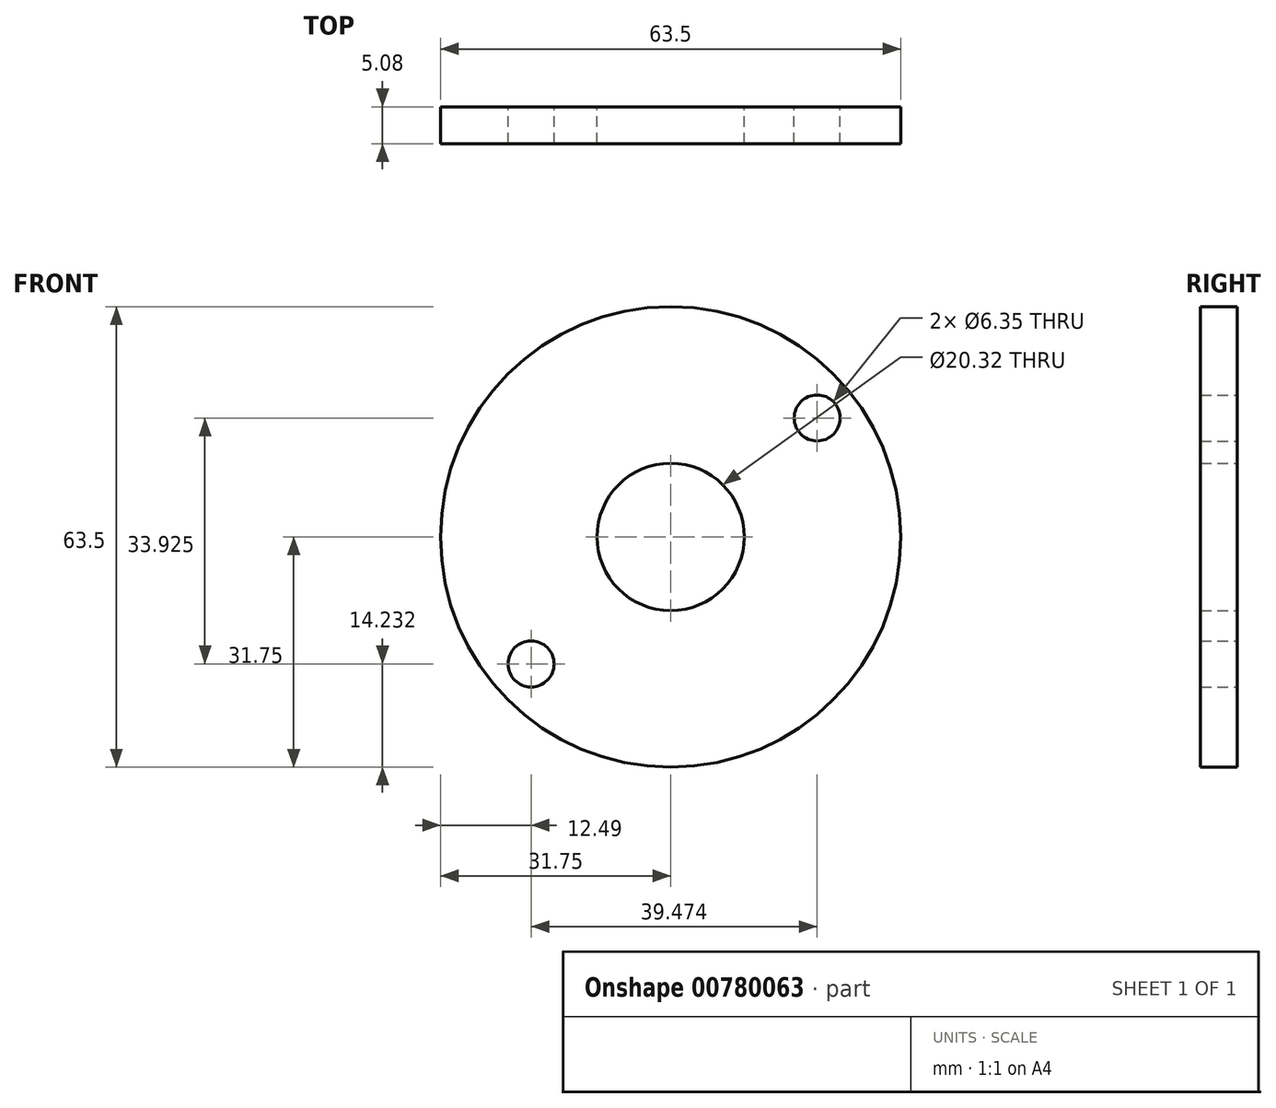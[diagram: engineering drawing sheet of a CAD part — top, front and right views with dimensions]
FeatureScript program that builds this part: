
annotation { "Feature Type Name" : "Feature", "Feature Type Description" : "" }
export const myFeature = defineFeature(function(context is Context, id is Id, definition is map)
    precondition{}
    {
        {
            var Q0;
            Q0=qCreatedBy(makeId("Front.planeOp"),FACE);
            var sketch = newSketch(context, id + "F0", { "sketchPlane" : qUnion([Q0])});
            skCircle(sketch, "E0", {"center": v(0, 0) * mm, "radius": 31.75 * mm});
            skCircle(sketch, "E1", {"center": v(0, 0) * mm, "radius": 10.16 * mm});
            skCircle(sketch, "E2", {"center": v(20.21, 16.4) * mm, "radius": 3.18 * mm});
            skCircle(sketch, "E3", {"center": v(-19.26, -17.52) * mm, "radius": 3.18 * mm});
            skSolve(sketch);
        }
        {
            var Q0;
            Q0=makeQuery(id+"F0.imprint","IMPRINT",FACE,{"disambiguationData":[TD([[makeQuery(id+"F0.imprint","IMPRINT",EDGE,{"derivedFrom":sQuery(id+"F0.wireOp",EDGE,"E0")}),1.0]])]});
            extrude(context, id + "F1", {"entities" : qUnion([Q0]), "depth" : 5.08 * mm, "offsetDistance" : 25.4 * mm});
        }
    });
